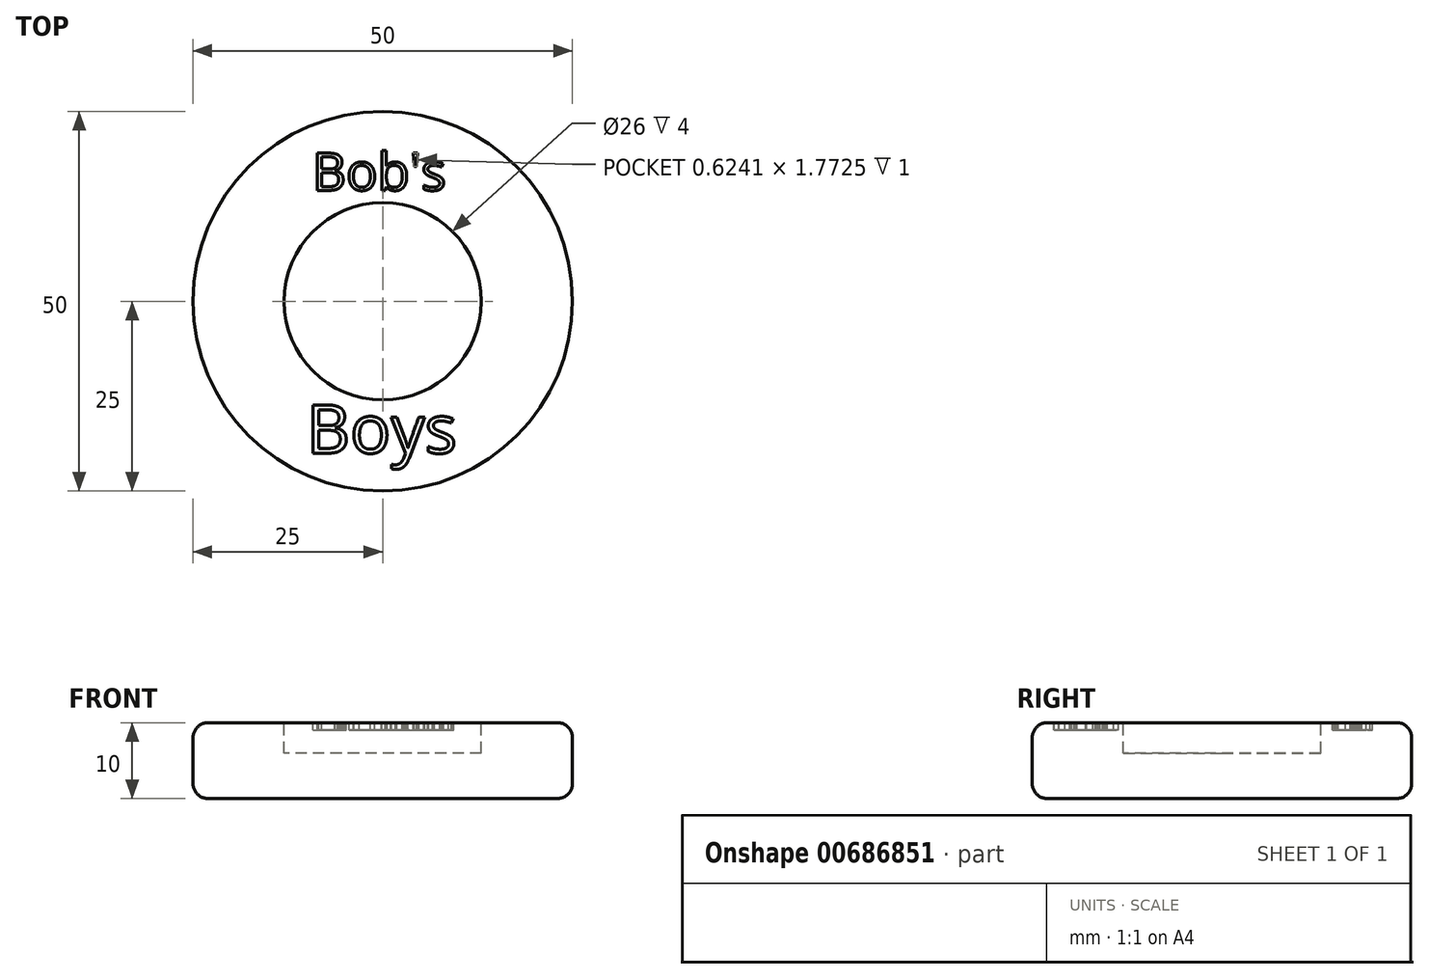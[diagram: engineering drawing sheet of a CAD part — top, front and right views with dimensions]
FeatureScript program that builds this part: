
annotation { "Feature Type Name" : "Feature", "Feature Type Description" : "" }
export const myFeature = defineFeature(function(context is Context, id is Id, definition is map)
    precondition{}
    {
        {
            var Q0;
            Q0=qCreatedBy(makeId("Top.planeOp"),FACE);
            var sketch = newSketch(context, id + "F0", { "sketchPlane" : qUnion([Q0])});
            skCircle(sketch, "E0", {"center": v(0, 0) * mm, "radius": 25 * mm});
            skSolve(sketch);
        }
        {
            var Q0;
            Q0=qSketchRegion(id+"F0",true);
            extrude(context, id + "F1", {"entities" : qUnion([Q0]), "depth" : 10 * mm, "offsetDistance" : 25 * mm});
        }
        {
            var Q0;
            Q0=makeQuery(id+"F1.opExtrude","CAP_EDGE",EDGE,{"disambiguationData":[OSD([sQuery(id+"F0.wireOp",EDGE,"E0")])],"isStart":false});
            var Q1;
            Q1=makeQuery(id+"F1.opExtrude","CAP_EDGE",EDGE,{"disambiguationData":[OSD([sQuery(id+"F0.wireOp",EDGE,"E0")])],"isStart":true});
            fillet(context, id + "F2", {"entities" : qUnion([Q0, Q1]), "radius" : 2 * mm, "tangentPropagation" : true, "allowEdgeOverflow" : false});
        }
        {
            var Q0;
            Q0=makeQuery(id+"F1.opExtrude","CAP_FACE",FACE,{"disambiguationData":[OSD([sQuery(id+"F0.wireOp",EDGE,"E0")])],"isStart":false});
            var sketch = newSketch(context, id + "F3", { "sketchPlane" : qUnion([Q0])});
            skCircle(sketch, "E1", {"center": v(0, 0) * mm, "radius": 13 * mm});
            skSolve(sketch);
        }
        {
            var Q0;
            Q0=sQuery(id+"F3.wireOp",VERTEX,"E1.center");
            var Q1;
            Q1=makeQuery(id+"F1.opExtrude","SWEPT_BODY",BODY,{"disambiguationData":[OSD([sQuery(id+"F0.wireOp",EDGE,"E0")])]});
            hole(context, id + "F4", {"style" : HoleStyle.SIMPLE, "endStyle" : HoleEndStyle.THROUGH, "holeDiameter" : 26 * mm, "majorDiameter" : 5 * mm, "isTappedThrough" : true, "tappedDepth" : 12 * mm, "tapClearance" : 3, "locations" : qUnion([Q0]), "scope" : qUnion([Q1])});
        }
        {
            var Q0;
            Q0=makeQuery(id+"F1.opExtrude","CAP_FACE",FACE,{"disambiguationData":[OSD([sQuery(id+"F0.wireOp",EDGE,"E0")])],"isStart":true});
            var sketch = newSketch(context, id + "F5", { "sketchPlane" : qUnion([Q0])});
            skCircle(sketch, "E2", {"center": v(0, 0) * mm, "radius": 13 * mm});
            skSolve(sketch);
        }
        {
            var Q0;
            Q0 = qSketchRegion(id + "F5", true);
            extrude(context, id + "F6", {"entities" : qUnion([Q0]), "operationType" : NewBodyOperationType.ADD, "oppositeDirection" : true, "depth" : 6 * mm, "offsetDistance" : 25 * mm});
        }
        {
            var Q0;
            Q0=makeQuery(id+"F1.opExtrude","CAP_FACE",FACE,{"disambiguationData":[OSD([sQuery(id+"F0.wireOp",EDGE,"E0")])],"isStart":false});
            var sketch = newSketch(context, id + "F7", { "sketchPlane" : qUnion([Q0])});
            skText(sketch, "E3", { "text": "Bob\'s", "fontName": "OpenSans-Regular.ttf"});
            skText(sketch, "E4", { "text": "Boys", "fontName": "OpenSans-Regular.ttf"});
            const initialGuessF7  = {"E3": [-0.00928, 0.01461, 1, 0, 0.00495], "E4": [-0.01007, -0.02, 1, 0, 0.0064]};
            skSetInitialGuess(sketch, initialGuessF7);
            skSolve(sketch);
        }
        {
            var Q0;
            Q0 = qSketchRegion(id + "F7", true);
            extrude(context, id + "F8", {"entities" : qUnion([Q0]), "operationType" : NewBodyOperationType.REMOVE, "oppositeDirection" : true, "depth" : 1 * mm, "offsetDistance" : 25 * mm});
        }
    });
